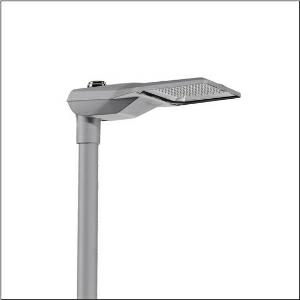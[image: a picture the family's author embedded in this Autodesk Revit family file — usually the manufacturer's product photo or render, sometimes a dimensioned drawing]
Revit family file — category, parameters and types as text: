
# Revit family: streetlight_sl_21_midi___p1_0a_5xe7a37n08lb_cb5e
name_source: partatom
category: Lighting Fixtures
units: mm (PartAtom-declared; Revit-internal decimal feet)

## family parameters
Cut with Voids When Loaded = No
Host = Face
Light Source = No
Part Type = Normal
Room Calculation Point = No
Round Connector Dimension = Use Diameter
Shared = No

## types (1)
- --- (1 x LED, 14340 lm, 98.3 W, 3000K)
    Apparent Load = 98 VA
    CIE Flux Codes = 21 50 90 100 100
    Color Rendering = 70
    Color Temperature = 3000K
    Default Elevation = 1800 mm
    Description = Streetlight SL 21 midi, mast luminaire, primary light control with lens, of PMMA, primary optical cover: cover, of toughened safety glass, transparent, light distribution: P1.0a, light emission: direct distribution, primary light characteristic: asymmetric, installation type: side-entry, LED, 3G 2.5mm², High Power LED, rated luminous flux: 14.340lm, luminous efficacy: 146lm/W, light colour: 730, colour temperature: 3000K, control gear: NEMA (7pin), control: overheat protection, pre-setting: linear dimming characteristic, constant luminous flux control, time-dependent luminous flux control, flexible luminous flux parameterisation, mains connection: 220..240V, AC, 50/60Hz, connection cable pre-assembled, cable length: 10,5m, wiring characteristics: H05VV-F, start of lifetime: 98W, end of service life: 101W, reduction: 45W, luminaire housing, of diecast aluminium (EN AC-44300), powder-coated, Siteco® metallic grey (DB 702S), corrosivity category C5 mid according to DIN EN ISO 12944, multi-level sealing system, sealing non-destructively replaceable, inclination adjustable: 0°, 5°, 10°, 15°, length: 644mm, width: 335mm, height: 110mm, spigot size: 42mm (side-entry), mounting height: 4..8m, protection rating (complete): IP66, insulation class (complete): insulation class I (protective earthing), certification: CE, ENEC, ENEC+, VDE, impact resistance: IK10, permissible operating ambient temperature for outdoor applications: -40..+50°C, standard-compliant lighting for roads and squares, packaging unit: 1 piece

Light Distribution: P1.0a
    Height = 111 mm
    Lamp = 1 x LED
    Lamp Light Flux = 14340 lm
    Lamp Power = 98.3 W
    Lamp count = 1
    Length = 644 mm
    Luminous efficacy = 146 lm/W
    Manufacturer = Siteco
    ModVariant = No
    Model = 5XE7A37N08LB
    Number of Poles = 1
    OnlyDefault = Yes
    Power Factor = 1
    Product Name = Streetlight SL 21 midi | P1.0a
    Product group = mast luminaire | pylon top
    ProductGroupID = 6100
    Protection Class = Protection class I
    Protection Degree = IP 66
    RLX_Detail_Level = 1
    RLX_Emergency_Light_Flux = 0 lm
    RLX_Emergency_Type = 0
    RLX_Emergency_Type_DB = No
    RlxData = <blob elided: 37913 chars, md5=2fc9314e>
    Socket = socket
    Standby Power = 0 W
    System Light Flux = 14340 lm
    System Power = 98 W
    Type Comments = factory setting: luminous flux: 100 % | dim-lin: 254 | 1020 mA
    Type Image = l_1294377.jpg
    URL = http://relux.com
    VarID = @adj_134560
    Voltage = 0 V
    Weight = 0.00 kg
    Width = 336 mm

## geometry (parser evidence)
native form markers: Blend x4, Sweep x12
no freeform markers — native parametric forms only
